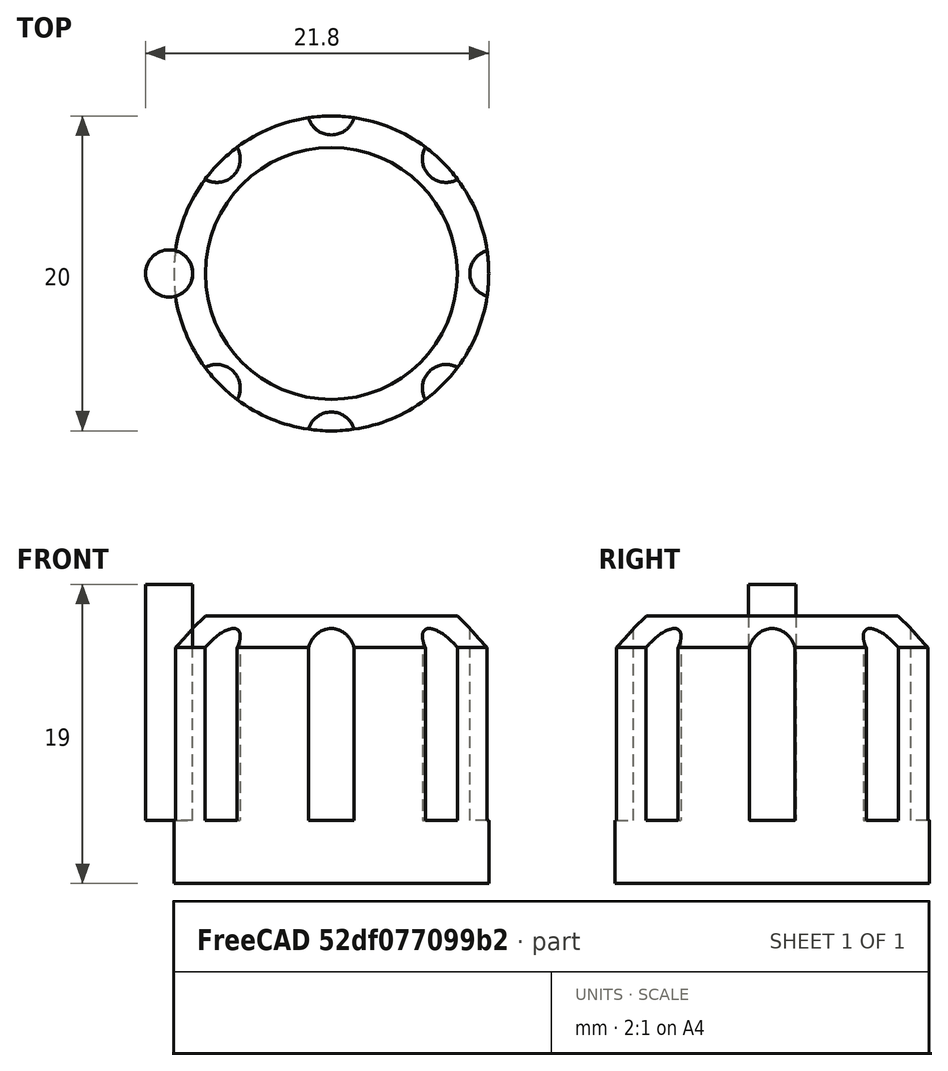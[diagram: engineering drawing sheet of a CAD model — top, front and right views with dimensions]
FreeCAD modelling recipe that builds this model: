
FCSTD DOCUMENT  (FreeCAD 0.21R33694 (Git))
Label: OJT1_T12R01_xamfransboto
License: All rights reserved
LicenseURL: https://en.wikipedia.org/wiki/All_rights_reserved
objects: Part::Cylinder×2, Part::Chamfer×1, Part::FeaturePython×1, Part::Cut×1
note: 4 computed .brp shape members not serialized (recipe doc carries the construction recipe); baked Part::Feature solids carry a one-line shape summary decoded from their .brp

FEATURE [Part::Cylinder] Cylinder  label="Cilindre_gran"
  Angle = 360
  AttacherType = Attacher::AttachEngine3D
  FirstAngle = 0
  Height = 17
  Placement = pos=(10.5,0,8) rot=(0,0,1;0rad)
  Radius = 10
  SecondAngle = 0
FEATURE [Part::Chamfer] Chamfer
  Base = -> Cylinder
  Edges = 1 edges r=2: [Edge3]
FEATURE [Part::Cylinder] Cylinder001  label="Cilindre"
  Angle = 360
  AttacherType = Attacher::AttachEngine3D
  FirstAngle = 0
  Height = 15
  Placement = pos=(0.2,0,12) rot=(0,0,1;0rad)
  Radius = 1.5
  SecondAngle = 0
FEATURE [Part::FeaturePython] Array  # Draft array (typed FeaturePython)
  AlwaysSyncPlacement = false
  Angle = 360
  ArrayType = 1
  Axis = (0,0,1)
  Base = -> Cylinder001
  Center = (10.5,0,0)
  Count = 8
  ExpandArray = false
  Fuse = false
  IntervalAxis = (0,0,0)
  IntervalX = (100,0,0)
  IntervalY = (0,100,0)
  IntervalZ = (0,0,100)
  NumberCircles = 3
  NumberPolar = 8
  NumberX = 2
  NumberY = 2
  NumberZ = 1
  PlacementList = 8 placements: [(0.2,0,12),(3.2168,-7.2832,12),(10.5,-10.3,12),(17.7832,-7.2832,12),(20.8,-1.26139e-15,12),(17.7832,7.2832,12),(10.5,10.3,12),(3.2168,7.2832,12)]
  RadialDistance = 50
  ScaleList = (8) [(1,1,1),(1,1,1),(1,1,1),(1,1,1),(1,1,1),(1,1,1),(1,1,1),(1,1,1)]
  Symmetry = 1
  TangentialDistance = 25
FEATURE [Part::Cut] Cut
  Base = -> Chamfer
  Tool = -> Array
